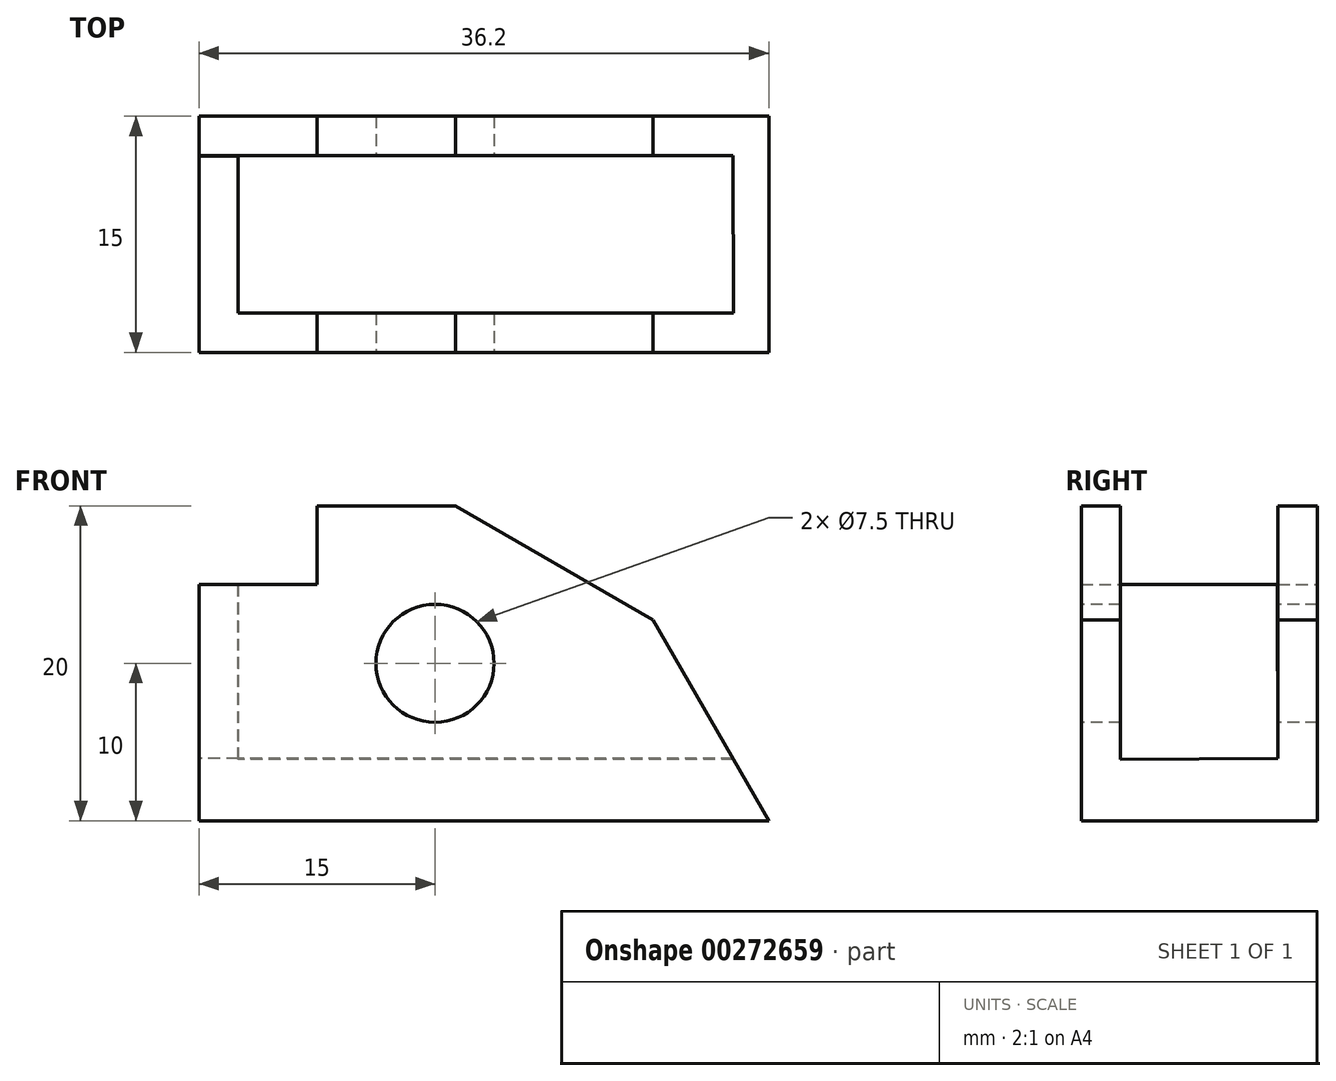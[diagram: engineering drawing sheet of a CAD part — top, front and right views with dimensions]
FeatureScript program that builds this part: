
annotation { "Feature Type Name" : "Feature", "Feature Type Description" : "" }
export const myFeature = defineFeature(function(context is Context, id is Id, definition is map)
    precondition{}
    {
        {
            var Q0;
            Q0=qCreatedBy(makeId("Front.planeOp"),FACE);
            var sketch = newSketch(context, id + "F0", { "sketchPlane" : qUnion([Q0])});
            skLineSegment(sketch, "E0", {"start": v(0, 0) * mm, "end": v(0, 15) * mm});
            skLineSegment(sketch, "E1", {"start": v(0, 15) * mm, "end": v(7.5, 15) * mm});
            skLineSegment(sketch, "E2", {"start": v(7.5, 15) * mm, "end": v(7.5, 20) * mm});
            skLineSegment(sketch, "E3", {"start": v(7.5, 20) * mm, "end": v(16.3, 20) * mm});
            skLineSegment(sketch, "E4", {"start": v(36.2, 0) * mm, "end": v(0, 0) * mm});
            skPoint(sketch, "E5.start.orphan", {"position": v(27.54, 15) * mm});
            skLineSegment(sketch, "E6", {"start": v(16.3, 20) * mm, "end": v(28.83, 12.77) * mm});
            skLineSegment(sketch, "E7", {"start": v(28.83, 12.77) * mm, "end": v(36.2, 0) * mm});
            skSolve(sketch);
        }
        {
            var Q0;
            Q0=makeQuery(id+"F0.imprint","IMPRINT",FACE,{"disambiguationData":[TD([[makeQuery(id+"F0.imprint","IMPRINT",EDGE,{"derivedFrom":sQuery(id+"F0.wireOp",EDGE,"E0")}),-1.0]])]});
            extrude(context, id + "F1", {"entities" : qUnion([Q0]), "depth" : 15 * mm});
        }
        {
            var Q0;
            Q0=makeQuery(id+"F1.opExtrude","SWEPT_FACE",FACE,{"disambiguationData":[OSD([sQuery(id+"F0.wireOp",EDGE,"E0")])]});
            var sketch = newSketch(context, id + "F2", { "sketchPlane" : qUnion([Q0])});
            skLineSegment(sketch, "E8", {"start": v(2.5, 3.95) * mm, "end": v(2.5, 21.57) * mm});
            skLineSegment(sketch, "E9", {"start": v(12.5, 3.9) * mm, "end": v(2.5, 3.95) * mm});
            skLineSegment(sketch, "E10", {"start": v(12.5, 3.9) * mm, "end": v(12.5, 21.57) * mm});
            skPoint(sketch, "E11.end.orphan", {"position": v(11.98, 21.57) * mm});
            skLineSegment(sketch, "E12", {"start": v(2.5, 21.57) * mm, "end": v(12.5, 21.57) * mm});
            skSolve(sketch);
        }
        {
            var Q0;
            {var subQ0=sQuery(id+"F2.wireOp",EDGE,"E9");Q0=makeQuery(id+"F2.imprint","IMPRINT",FACE,{"disambiguationData":[TD([[makeQuery(id+"F2.imprint","IMPRINT",EDGE,{"derivedFrom":subQ0}),-1.0]])]});}
            var Q1;
            {var subQ0=sQuery(id+"F2.wireOp",EDGE,"E12");Q1=makeQuery(id+"F2.imprint","IMPRINT",FACE,{"disambiguationData":[TD([[makeQuery(id+"F2.imprint","IMPRINT",EDGE,{"derivedFrom":subQ0}),-1.0]])]});}
            extrude(context, id + "F3", {"entities" : qUnion([Q0, Q1]), "operationType" : NewBodyOperationType.REMOVE, "oppositeDirection" : true, "depth" : 40 * mm});
        }
        {
            var Q0;
            Q0=makeQuery(id+"F3.boolean.opBoolean","COPY",FACE,{"derivedFrom":makeQuery(id+"F3.opExtrude","SWEPT_FACE",FACE,{"disambiguationData":[OSD([sQuery(id+"F2.wireOp",EDGE,"E9")])]})});
            var sketch = newSketch(context, id + "F4", { "sketchPlane" : qUnion([Q0])});
            skLineSegment(sketch, "E13.bottom", {"start": v(0, -2.48) * mm, "end": v(2.5, -2.48) * mm});
            skLineSegment(sketch, "E13.top", {"start": v(0, -12.48) * mm, "end": v(2.5, -12.48) * mm});
            skLineSegment(sketch, "E13.left", {"start": v(0, -2.48) * mm, "end": v(0, -12.48) * mm});
            skLineSegment(sketch, "E13.right", {"start": v(2.5, -2.48) * mm, "end": v(2.5, -12.48) * mm});
            skSolve(sketch);
        }
        {
            var Q0;
            Q0 = qSketchRegion(id + "F4", true);
            var Q1;
            {var subQ2=sQuery(id+"F0.wireOp",EDGE,"E1");Q1=makeQuery(id+"F3.boolean.opBoolean","SPLIT",FACE,{"disambiguationData":[TD([makeQuery(id+"F3.opExtrude","SWEPT_FACE",FACE,{"disambiguationData":[OSD([sQuery(id+"F2.wireOp",EDGE,"E8")])]})])],"derivedFrom":makeQuery(id+"F1.opExtrude","SWEPT_FACE",FACE,{"disambiguationData":[OSD([subQ2])]})});}
            extrude(context, id + "F5", {"entities" : qUnion([Q0]), "operationType" : NewBodyOperationType.ADD, "endBound" : BoundingType.UP_TO_SURFACE, "endBoundEntityFace" : qUnion([Q1]), "depth" : 25 * mm});
        }
        {
            var Q0;
            Q0=makeQuery(id+"F1.opExtrude","CAP_FACE",FACE,{"disambiguationData":[OSD([sQuery(id+"F0.wireOp",EDGE,"E0"),sQuery(id+"F0.wireOp",EDGE,"E1"),sQuery(id+"F0.wireOp",EDGE,"E2"),sQuery(id+"F0.wireOp",EDGE,"E3"),sQuery(id+"F0.wireOp",EDGE,"E4"),sQuery(id+"F0.wireOp",EDGE,"E6"),sQuery(id+"F0.wireOp",EDGE,"E7")])],"isStart":false});
            var sketch = newSketch(context, id + "F6", { "sketchPlane" : qUnion([Q0])});
            skCircle(sketch, "E14", {"center": v(15, 10) * mm, "radius": 3.75 * mm});
            skSolve(sketch);
        }
        {
            var Q0;
            Q0=makeQuery(id+"F6.imprint","IMPRINT",FACE,{"disambiguationData":[TD([[makeQuery(id+"F6.imprint","IMPRINT",EDGE,{"derivedFrom":sQuery(id+"F6.wireOp",EDGE,"E14")}),1.0]])]});
            extrude(context, id + "F7", {"entities" : qUnion([Q0]), "operationType" : NewBodyOperationType.REMOVE, "oppositeDirection" : true, "depth" : 25 * mm});
        }
    });
